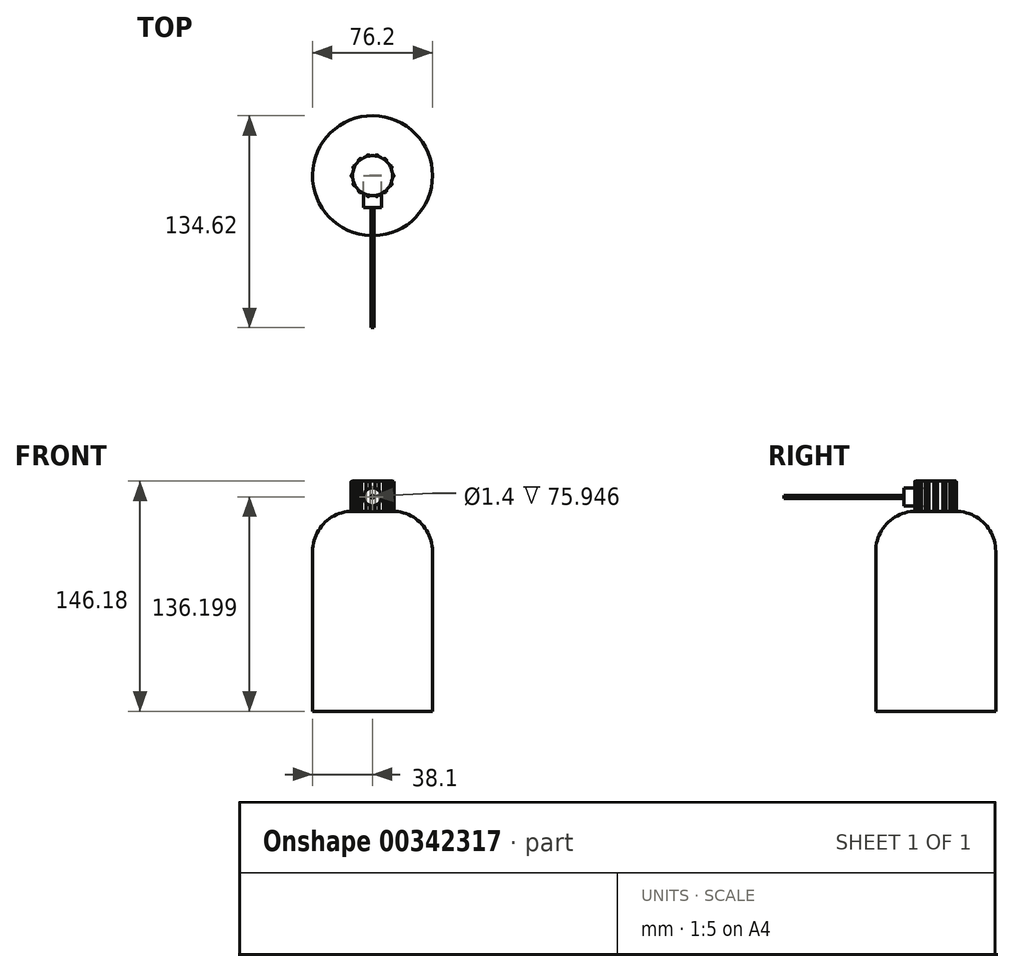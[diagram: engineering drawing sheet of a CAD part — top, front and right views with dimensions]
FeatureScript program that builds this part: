
annotation { "Feature Type Name" : "Feature", "Feature Type Description" : "" }
export const myFeature = defineFeature(function(context is Context, id is Id, definition is map)
    precondition{}
    {
        {
            var Q0;
            Q0=qCreatedBy(makeId("Top.planeOp"),FACE);
            var sketch = newSketch(context, id + "F0", { "sketchPlane" : qUnion([Q0])});
            skCircle(sketch, "E0", {"center": v(0, 0) * mm, "radius": 38.1 * mm});
            skSolve(sketch);
        }
        {
            var Q0;
            Q0=makeQuery(id+"F0.imprint","IMPRINT",FACE,{"disambiguationData":[TD([[makeQuery(id+"F0.imprint","IMPRINT",EDGE,{"derivedFrom":sQuery(id+"F0.wireOp",EDGE,"E0")}),1.0]])]});
            extrude(context, id + "F1", {"entities" : qUnion([Q0]), "depth" : 63.5 * mm, "hasSecondDirection" : true, "secondDirectionOppositeDirection" : true, "secondDirectionDepth" : 63.5 * mm});
        }
        {
            var Q0;
            Q0=makeQuery(id+"F1.opExtrude","CAP_FACE",FACE,{"disambiguationData":[OSD([sQuery(id+"F0.wireOp",EDGE,"E0")])],"isStart":false});
            fillet(context, id + "F2", {"entities" : qUnion([Q0]), "radius" : 25.4 * mm, "tangentPropagation" : true, "allowEdgeOverflow" : false});
        }
        {
            var Q0;
            Q0=makeQuery(id+"F1.opExtrude","CAP_FACE",FACE,{"disambiguationData":[OSD([sQuery(id+"F0.wireOp",EDGE,"E0")])],"isStart":false});
            var sketch = newSketch(context, id + "F3", { "sketchPlane" : qUnion([Q0])});
            skCircle(sketch, "E1", {"center": v(0, 0) * mm, "radius": 12.7 * mm});
            skSolve(sketch);
        }
        {
            var Q0;
            Q0=makeQuery(id+"F3.imprint","IMPRINT",FACE,{"disambiguationData":[TD([[makeQuery(id+"F3.imprint","IMPRINT",EDGE,{"derivedFrom":sQuery(id+"F3.wireOp",EDGE,"E1")}),1.0]])]});
            extrude(context, id + "F4", {"entities" : qUnion([Q0]), "operationType" : NewBodyOperationType.ADD, "depth" : 19.18 * mm});
        }
        {
            var Q0;
            Q0=qCreatedBy(makeId("Top.planeOp"),FACE);
            cPlane(context, id + "F5", {"entities" : qUnion([Q0]), "cplaneType" : CPlaneType.OFFSET, "offset" : 63.5 * mm, "width" : 152.4 * mm, "height" : 152.4 * mm});
        }
        {
            var Q0;
            Q0=qCreatedBy(id+"F5.planeOp",FACE);
            var sketch = newSketch(context, id + "F6", { "sketchPlane" : qUnion([Q0])});
            skCircle(sketch, "E2", {"center": v(12.25, 0) * mm, "radius": 1.27 * mm});
            skSolve(sketch);
        }
        {
            var Q0;
            Q0=makeQuery(id+"F6.imprint","IMPRINT",FACE,{"disambiguationData":[TD([[makeQuery(id+"F6.imprint","IMPRINT",EDGE,{"derivedFrom":sQuery(id+"F6.wireOp",EDGE,"E2")}),1.0]])]});
            extrude(context, id + "F7", {"entities" : qUnion([Q0]), "depth" : 19.05 * mm});
        }
        {
            var Q0;
            Q0=qCreatedBy(makeId("Front.planeOp"),FACE);
            var sketch = newSketch(context, id + "F8", { "sketchPlane" : qUnion([Q0])});
            skLineSegment(sketch, "E3", {"start": v(0, 32.27) * mm, "end": v(0, 107.15) * mm, "construction": true});
            skSolve(sketch);
        }
        {
            var Q0;
            Q0=makeQuery(id+"F7.opExtrude","SWEPT_BODY",BODY,{"disambiguationData":[OSD([sQuery(id+"F6.wireOp",EDGE,"E2")])]});
            var Q1;
            Q1=sQuery(id+"F8.wireOp",EDGE,"E3");
            circularPattern(context, id + "F9", {"operationType" : NewBodyOperationType.ADD, "entities" : qUnion([Q0]), "axis" : qUnion([Q1]), "angle" : 360 * degree, "instanceCount" : 14, "equalSpace" : true});
        }
        {
            var Q0;
            Q0=qCreatedBy(makeId("Front.planeOp"),FACE);
            var sketch = newSketch(context, id + "F10", { "sketchPlane" : qUnion([Q0])});
            skCircle(sketch, "E4", {"center": v(0, 72.7) * mm, "radius": 5.72 * mm});
            skSolve(sketch);
        }
        {
            var Q0;
            Q0 = qSketchRegion(id + "F10", true);
            extrude(context, id + "F11", {"entities" : qUnion([Q0]), "depth" : 20.32 * mm});
        }
        {
            var Q0;
            Q0=makeQuery(id+"F11.opExtrude","CAP_FACE",FACE,{"disambiguationData":[OSD([sQuery(id+"F10.wireOp",EDGE,"E4")])],"isStart":false});
            var sketch = newSketch(context, id + "F12", { "sketchPlane" : qUnion([Q0])});
            skCircle(sketch, "E5", {"center": v(0, 72.7) * mm, "radius": 0.95 * mm});
            skSolve(sketch);
        }
        {
            var Q0;
            Q0=makeQuery(id+"F12.imprint","IMPRINT",FACE,{"disambiguationData":[TD([[makeQuery(id+"F12.imprint","IMPRINT",EDGE,{"derivedFrom":sQuery(id+"F12.wireOp",EDGE,"E5")}),1.0]])]});
            extrude(context, id + "F13", {"entities" : qUnion([Q0]), "depth" : 76.2 * mm});
        }
        {
            var Q0;
            Q0=makeQuery(id+"F13.opExtrude","CAP_FACE",FACE,{"disambiguationData":[OSD([sQuery(id+"F12.wireOp",EDGE,"E5")])],"isStart":false});
            shell(context, id + "F14", {"entities" : qUnion([Q0]), "thickness" : 0.25 * mm});
        }
    });
